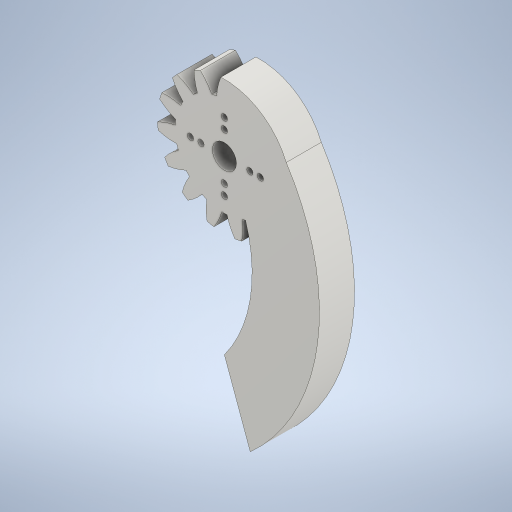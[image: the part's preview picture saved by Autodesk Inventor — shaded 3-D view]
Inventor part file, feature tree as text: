
AUTODESK INVENTOR PART (.ipt)
format: ipt  version: 2024 (Build 280153000, 153)  size: 853,504 bytes
history: native  units: mm (DEFAULTED — no unit token found)
features: other x7, extrude x3, plane x3, sketch x3, reference x1, projected_geometry x1
ambient origin geometry x8: Origin, YZ Plane, XZ Plane, XY Plane, X Axis, Y Axis, Z Axis, Center Point
bodies: Solid1 (feature_tree)
feature tree (18):
  extrude  "Extrusion1"  Depth=6.666667mm TaperAngle=0.0deg
  plane  "Work Plane2"
  plane  "Work Plane8"
  plane  "Work Plane9"
  other  "Spur Gear"
  extrude  "Extrusion2"  Depth=10.0mm TaperAngle=0.0deg
  extrude  "Extrusion3"  TaperAngle=0.0deg  [1 undecoded]
  sketch  "Sketch1"  dims[d0=25.49mm d1=6.666667mm d2=0.0mm]
  other  "Srf1"
  sketch  "Sketch3"  dims[d3=22.5mm d4=10.0mm d5=0.0mm]
  reference  "Reference1"
  sketch  "Sketch4"  dims[d16=23.4mm d17=0.0mm d34=2.094395mm d39=0.0mm d41=0.0mm d43=23.4mm d46=23.4mm d47=0.0mm d48=0.0mm d49=10.0mm d50=0.0mm d51=50.0mm d52=79.653867mm d53=54.037661mm d54=6.666667mm d55=0.0mm d61=3.490659mm d62=21.741525mm d63=27.373048mm d65=4.85mm d66=16.630991mm]
  projected_geometry  "Projected Loop1"
  other  "Pitch Diameter"
  other  "<userpath> windows\Documents\Inventor\Robotska_roka\roka_asemb.iam"
  other  "roka_asemb.iam"
  other  "SG90 - Micro Servo 9g - Tower Pro:2"
  other  "SG90 - Micro Servo 9g - Tower Pro.4"
note: 1 required parameter value undecoded (feature->parameter linkage not recoverable at this tier; creation-order binding heuristic only, values carry confidence <= 0.55)
